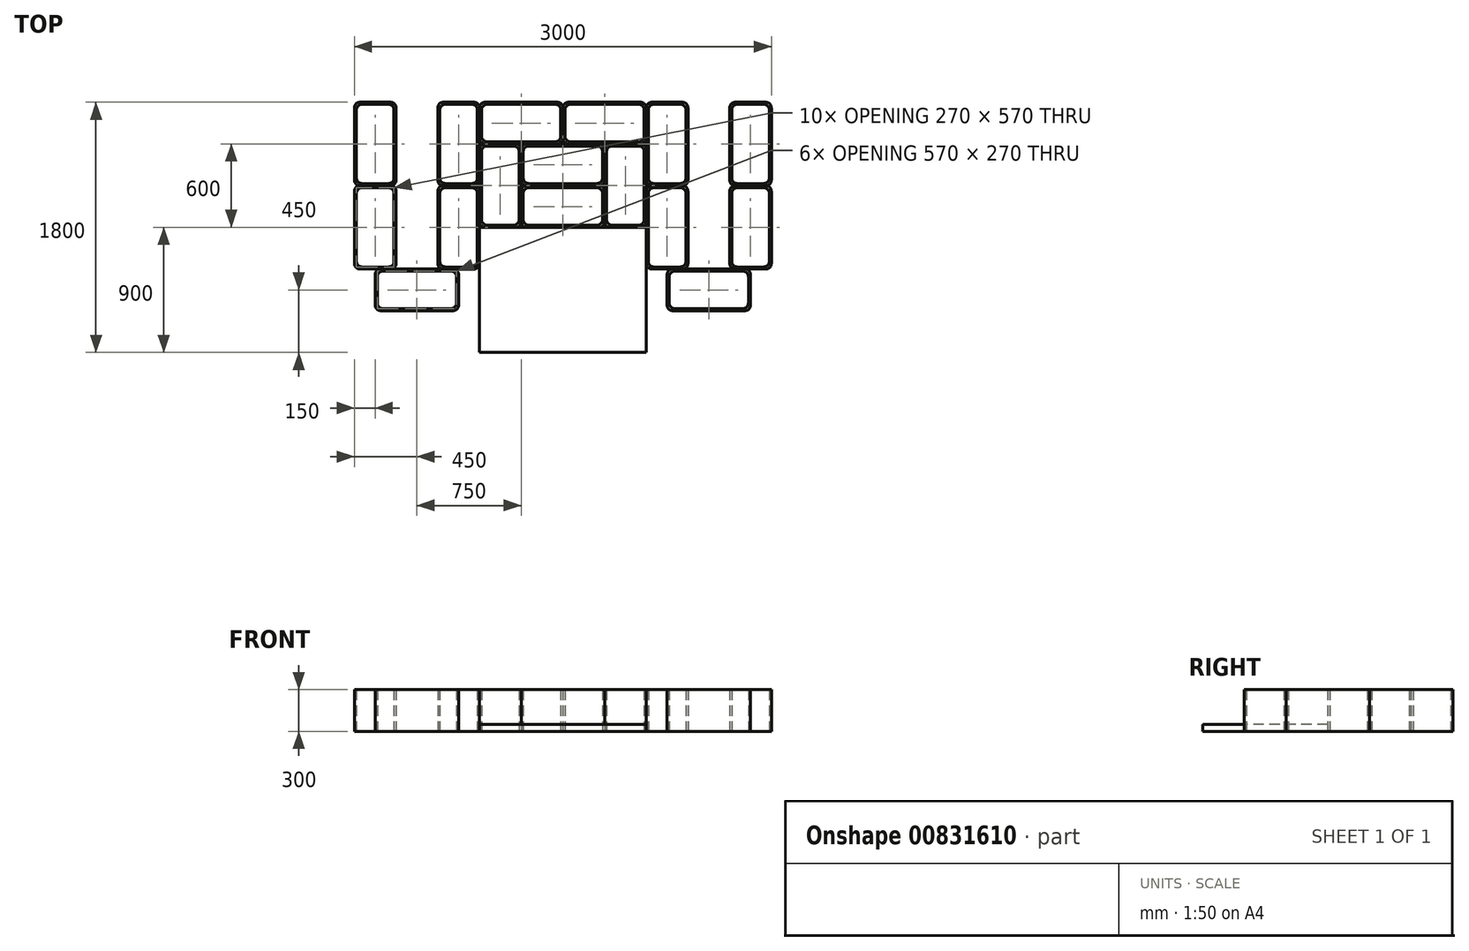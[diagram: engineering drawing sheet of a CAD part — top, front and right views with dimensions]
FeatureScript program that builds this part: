
annotation { "Feature Type Name" : "Feature", "Feature Type Description" : "" }
export const myFeature = defineFeature(function(context is Context, id is Id, definition is map)
    precondition{}
    {
        {
            var Q0;
            Q0=qCreatedBy(makeId("Top.planeOp"),FACE);
            var sketch = newSketch(context, id + "F0", { "sketchPlane" : qUnion([Q0])});
            skLineSegment(sketch, "E0.bottom", {"start": v(260, 150) * mm, "end": v(-260, 150) * mm});
            skLineSegment(sketch, "E0.top", {"start": v(260, -150) * mm, "end": v(-260, -150) * mm});
            skLineSegment(sketch, "E0.left", {"start": v(300, 110) * mm, "end": v(300, -110) * mm});
            skLineSegment(sketch, "E0.right", {"start": v(-300, 110) * mm, "end": v(-300, -110) * mm});
            skPoint(sketch, "E0.middle", {"position": v(0, 0) * mm});
            skArc(sketch, "E1", {"start": v(-300, -110) * mm, "mid": v(-288.28, -138.28) * mm, "end": v(-260, -150) * mm});
            skArc(sketch, "E2", {"start": v(260, -150) * mm, "mid": v(288.28, -138.28) * mm, "end": v(300, -110) * mm});
            skArc(sketch, "E3", {"start": v(300, 110) * mm, "mid": v(288.28, 138.28) * mm, "end": v(260, 150) * mm});
            skArc(sketch, "E4", {"start": v(-260, 150) * mm, "mid": v(-288.28, 138.28) * mm, "end": v(-300, 110) * mm});
            skPoint(sketch, "E5.orphan", {"position": v(-300, -150) * mm});
            skPoint(sketch, "E6.orphan", {"position": v(300, -150) * mm});
            skPoint(sketch, "E7.orphan", {"position": v(300, 150) * mm});
            skPoint(sketch, "E8.orphan", {"position": v(-300, 150) * mm});
            skSolve(sketch);
        }
        {
            var Q0;
            Q0=makeQuery(id+"F0.imprint","IMPRINT",FACE,{"disambiguationData":[TD([[makeQuery(id+"F0.imprint","IMPRINT",EDGE,{"derivedFrom":sQuery(id+"F0.wireOp",EDGE,"E0.bottom")}),1.0]])]});
            var sketch = newSketch(context, id + "F1", { "sketchPlane" : qUnion([Q0])});
            skLineSegment(sketch, "E9.bottom", {"start": v(245, 135) * mm, "end": v(-245, 135) * mm});
            skLineSegment(sketch, "E9.top", {"start": v(245, -135) * mm, "end": v(-245, -135) * mm});
            skLineSegment(sketch, "E9.left", {"start": v(285, 95) * mm, "end": v(285, -95) * mm});
            skLineSegment(sketch, "E9.right", {"start": v(-285, 95) * mm, "end": v(-285, -95) * mm});
            skPoint(sketch, "E9.middle", {"position": v(0, 0) * mm});
            skArc(sketch, "E10", {"start": v(-285, -95) * mm, "mid": v(-273.28, -123.28) * mm, "end": v(-245, -135) * mm});
            skArc(sketch, "E11", {"start": v(245, -135) * mm, "mid": v(273.28, -123.28) * mm, "end": v(285, -95) * mm});
            skPoint(sketch, "E12.orphan", {"position": v(-285, -135) * mm});
            skPoint(sketch, "E13.orphan", {"position": v(285, -135) * mm});
            skArc(sketch, "E14", {"start": v(285, 95) * mm, "mid": v(273.28, 123.28) * mm, "end": v(245, 135) * mm});
            skArc(sketch, "E15", {"start": v(-245, 135) * mm, "mid": v(-273.28, 123.28) * mm, "end": v(-285, 95) * mm});
            skPoint(sketch, "E16.orphan", {"position": v(285, 135) * mm});
            skPoint(sketch, "E17.orphan", {"position": v(-285, 135) * mm});
            skSolve(sketch);
        }
        {
            var Q0;
            Q0=makeQuery(id+"F1.imprint","IMPRINT",FACE,{"disambiguationData":[TD([[makeQuery(id+"F1.imprint","IMPRINT",EDGE,{"derivedFrom":sQuery(id+"F1.wireOp",EDGE,"E9.bottom")}),-1.0]])]});
            extrude(context, id + "F2", {"entities" : qUnion([Q0]), "depth" : 300 * mm, "offsetDistance" : 25 * mm});
        }
        {
            var Q0;
            Q0=makeQuery(id+"F2.opExtrude","SWEPT_BODY",BODY,{"disambiguationData":[OSD([sQuery(id+"F0.wireOp",EDGE,"E0.bottom"),sQuery(id+"F0.wireOp",EDGE,"E0.top"),sQuery(id+"F0.wireOp",EDGE,"E0.left"),sQuery(id+"F0.wireOp",EDGE,"E0.right"),sQuery(id+"F0.wireOp",EDGE,"E1"),sQuery(id+"F0.wireOp",EDGE,"E2"),sQuery(id+"F0.wireOp",EDGE,"E3"),sQuery(id+"F0.wireOp",EDGE,"E4"),sQuery(id+"F1.wireOp",EDGE,"E9.bottom"),sQuery(id+"F1.wireOp",EDGE,"E9.top"),sQuery(id+"F1.wireOp",EDGE,"E9.left"),sQuery(id+"F1.wireOp",EDGE,"E9.right"),sQuery(id+"F1.wireOp",EDGE,"E10"),sQuery(id+"F1.wireOp",EDGE,"E11"),sQuery(id+"F1.wireOp",EDGE,"E14"),sQuery(id+"F1.wireOp",EDGE,"E15")])]});
            transform(context, id + "F3", {"entities" : qUnion([Q0]), "transformType" : TransformType.TRANSLATION_3D, "dx" : 900 * mm, "dy" : 0 * mm, "dz" : 0 * mm, "makeCopy" : true});
        }
        {
            var Q0;
            Q0=makeQuery(id+"F3.opPattern","COPY",BODY,{"derivedFrom":makeQuery(id+"F2.opExtrude","SWEPT_BODY",BODY,{"disambiguationData":[OSD([sQuery(id+"F0.wireOp",EDGE,"E0.bottom"),sQuery(id+"F0.wireOp",EDGE,"E0.top"),sQuery(id+"F0.wireOp",EDGE,"E0.left"),sQuery(id+"F0.wireOp",EDGE,"E0.right"),sQuery(id+"F0.wireOp",EDGE,"E1"),sQuery(id+"F0.wireOp",EDGE,"E2"),sQuery(id+"F0.wireOp",EDGE,"E3"),sQuery(id+"F0.wireOp",EDGE,"E4"),sQuery(id+"F1.wireOp",EDGE,"E9.bottom"),sQuery(id+"F1.wireOp",EDGE,"E9.top"),sQuery(id+"F1.wireOp",EDGE,"E9.left"),sQuery(id+"F1.wireOp",EDGE,"E9.right"),sQuery(id+"F1.wireOp",EDGE,"E10"),sQuery(id+"F1.wireOp",EDGE,"E11"),sQuery(id+"F1.wireOp",EDGE,"E14"),sQuery(id+"F1.wireOp",EDGE,"E15")])]}),"instanceName":"1"});
            var Q1;
            Q1=makeQuery(id+"F3.opPattern","COPY",EDGE,{"derivedFrom":makeQuery(id+"F2.opExtrude","SWEPT_EDGE",EDGE,{"disambiguationData":[OSD([sQuery(id+"F1.wireOp",EDGE,"E9.right"),sQuery(id+"F1.wireOp",EDGE,"E15")])]}),"instanceName":"1"});
            transform(context, id + "F4", {"entities" : qUnion([Q0]), "transformType" : TransformType.ROTATION, "transformAxis" : qUnion([Q1]), "angle" : 90 * degree, "makeCopy" : true});
        }
        {
            var Q0;
            Q0=makeQuery(id+"F4.opPattern","COPY",BODY,{"derivedFrom":makeQuery(id+"F3.opPattern","COPY",BODY,{"derivedFrom":makeQuery(id+"F2.opExtrude","SWEPT_BODY",BODY,{"disambiguationData":[OSD([sQuery(id+"F0.wireOp",EDGE,"E0.bottom"),sQuery(id+"F0.wireOp",EDGE,"E0.top"),sQuery(id+"F0.wireOp",EDGE,"E0.left"),sQuery(id+"F0.wireOp",EDGE,"E0.right"),sQuery(id+"F0.wireOp",EDGE,"E1"),sQuery(id+"F0.wireOp",EDGE,"E2"),sQuery(id+"F0.wireOp",EDGE,"E3"),sQuery(id+"F0.wireOp",EDGE,"E4"),sQuery(id+"F1.wireOp",EDGE,"E9.bottom"),sQuery(id+"F1.wireOp",EDGE,"E9.top"),sQuery(id+"F1.wireOp",EDGE,"E9.left"),sQuery(id+"F1.wireOp",EDGE,"E9.right"),sQuery(id+"F1.wireOp",EDGE,"E10"),sQuery(id+"F1.wireOp",EDGE,"E11"),sQuery(id+"F1.wireOp",EDGE,"E14"),sQuery(id+"F1.wireOp",EDGE,"E15")])]}),"instanceName":"1"}),"instanceName":"1"});
            transform(context, id + "F5", {"entities" : qUnion([Q0]), "transformType" : TransformType.TRANSLATION_3D, "dx" : -70 * mm, "dy" : 40 * mm, "dz" : 0 * mm, "makeCopy" : false});
        }
        {
            var Q0;
            Q0=makeQuery(id+"F3.opPattern","COPY",BODY,{"derivedFrom":makeQuery(id+"F2.opExtrude","SWEPT_BODY",BODY,{"disambiguationData":[OSD([sQuery(id+"F0.wireOp",EDGE,"E0.bottom"),sQuery(id+"F0.wireOp",EDGE,"E0.top"),sQuery(id+"F0.wireOp",EDGE,"E0.left"),sQuery(id+"F0.wireOp",EDGE,"E0.right"),sQuery(id+"F0.wireOp",EDGE,"E1"),sQuery(id+"F0.wireOp",EDGE,"E2"),sQuery(id+"F0.wireOp",EDGE,"E3"),sQuery(id+"F0.wireOp",EDGE,"E4"),sQuery(id+"F1.wireOp",EDGE,"E9.bottom"),sQuery(id+"F1.wireOp",EDGE,"E9.top"),sQuery(id+"F1.wireOp",EDGE,"E9.left"),sQuery(id+"F1.wireOp",EDGE,"E9.right"),sQuery(id+"F1.wireOp",EDGE,"E10"),sQuery(id+"F1.wireOp",EDGE,"E11"),sQuery(id+"F1.wireOp",EDGE,"E14"),sQuery(id+"F1.wireOp",EDGE,"E15")])]}),"instanceName":"1"});
            transform(context, id + "F6", {"entities" : qUnion([Q0]), "transformType" : TransformType.TRANSLATION_3D, "dx" : -1500 * mm, "dy" : 0 * mm, "dz" : 0 * mm, "makeCopy" : false});
        }
        {
            var Q0;
            Q0=makeQuery(id+"F3.opPattern","COPY",BODY,{"derivedFrom":makeQuery(id+"F2.opExtrude","SWEPT_BODY",BODY,{"disambiguationData":[OSD([sQuery(id+"F0.wireOp",EDGE,"E0.bottom"),sQuery(id+"F0.wireOp",EDGE,"E0.top"),sQuery(id+"F0.wireOp",EDGE,"E0.left"),sQuery(id+"F0.wireOp",EDGE,"E0.right"),sQuery(id+"F0.wireOp",EDGE,"E1"),sQuery(id+"F0.wireOp",EDGE,"E2"),sQuery(id+"F0.wireOp",EDGE,"E3"),sQuery(id+"F0.wireOp",EDGE,"E4"),sQuery(id+"F1.wireOp",EDGE,"E9.bottom"),sQuery(id+"F1.wireOp",EDGE,"E9.top"),sQuery(id+"F1.wireOp",EDGE,"E9.left"),sQuery(id+"F1.wireOp",EDGE,"E9.right"),sQuery(id+"F1.wireOp",EDGE,"E10"),sQuery(id+"F1.wireOp",EDGE,"E11"),sQuery(id+"F1.wireOp",EDGE,"E14"),sQuery(id+"F1.wireOp",EDGE,"E15")])]}),"instanceName":"1"});
            transform(context, id + "F7", {"entities" : qUnion([Q0]), "transformType" : TransformType.TRANSLATION_3D, "dx" : 300 * mm, "dy" : -300 * mm, "dz" : 0 * mm, "makeCopy" : true});
        }
        {
            var Q0;
            Q0=makeQuery(id+"F4.opPattern","COPY",BODY,{"derivedFrom":makeQuery(id+"F3.opPattern","COPY",BODY,{"derivedFrom":makeQuery(id+"F2.opExtrude","SWEPT_BODY",BODY,{"disambiguationData":[OSD([sQuery(id+"F0.wireOp",EDGE,"E0.bottom"),sQuery(id+"F0.wireOp",EDGE,"E0.top"),sQuery(id+"F0.wireOp",EDGE,"E0.left"),sQuery(id+"F0.wireOp",EDGE,"E0.right"),sQuery(id+"F0.wireOp",EDGE,"E1"),sQuery(id+"F0.wireOp",EDGE,"E2"),sQuery(id+"F0.wireOp",EDGE,"E3"),sQuery(id+"F0.wireOp",EDGE,"E4"),sQuery(id+"F1.wireOp",EDGE,"E9.bottom"),sQuery(id+"F1.wireOp",EDGE,"E9.top"),sQuery(id+"F1.wireOp",EDGE,"E9.left"),sQuery(id+"F1.wireOp",EDGE,"E9.right"),sQuery(id+"F1.wireOp",EDGE,"E10"),sQuery(id+"F1.wireOp",EDGE,"E11"),sQuery(id+"F1.wireOp",EDGE,"E14"),sQuery(id+"F1.wireOp",EDGE,"E15")])]}),"instanceName":"1"}),"instanceName":"1"});
            transform(context, id + "F8", {"entities" : qUnion([Q0]), "transformType" : TransformType.TRANSLATION_3D, "dx" : 300 * mm, "dy" : 0 * mm, "dz" : 0 * mm, "makeCopy" : true});
        }
        {
            var Q0;
            Q0=makeQuery(id+"F7.opPattern","COPY",BODY,{"derivedFrom":makeQuery(id+"F3.opPattern","COPY",BODY,{"derivedFrom":makeQuery(id+"F2.opExtrude","SWEPT_BODY",BODY,{"disambiguationData":[OSD([sQuery(id+"F0.wireOp",EDGE,"E0.bottom"),sQuery(id+"F0.wireOp",EDGE,"E0.top"),sQuery(id+"F0.wireOp",EDGE,"E0.left"),sQuery(id+"F0.wireOp",EDGE,"E0.right"),sQuery(id+"F0.wireOp",EDGE,"E1"),sQuery(id+"F0.wireOp",EDGE,"E2"),sQuery(id+"F0.wireOp",EDGE,"E3"),sQuery(id+"F0.wireOp",EDGE,"E4"),sQuery(id+"F1.wireOp",EDGE,"E9.bottom"),sQuery(id+"F1.wireOp",EDGE,"E9.top"),sQuery(id+"F1.wireOp",EDGE,"E9.left"),sQuery(id+"F1.wireOp",EDGE,"E9.right"),sQuery(id+"F1.wireOp",EDGE,"E10"),sQuery(id+"F1.wireOp",EDGE,"E11"),sQuery(id+"F1.wireOp",EDGE,"E14"),sQuery(id+"F1.wireOp",EDGE,"E15")])]}),"instanceName":"1"}),"instanceName":"1"});
            var Q1;
            Q1=makeQuery(id+"F4.opPattern","COPY",BODY,{"derivedFrom":makeQuery(id+"F3.opPattern","COPY",BODY,{"derivedFrom":makeQuery(id+"F2.opExtrude","SWEPT_BODY",BODY,{"disambiguationData":[OSD([sQuery(id+"F0.wireOp",EDGE,"E0.bottom"),sQuery(id+"F0.wireOp",EDGE,"E0.top"),sQuery(id+"F0.wireOp",EDGE,"E0.left"),sQuery(id+"F0.wireOp",EDGE,"E0.right"),sQuery(id+"F0.wireOp",EDGE,"E1"),sQuery(id+"F0.wireOp",EDGE,"E2"),sQuery(id+"F0.wireOp",EDGE,"E3"),sQuery(id+"F0.wireOp",EDGE,"E4"),sQuery(id+"F1.wireOp",EDGE,"E9.bottom"),sQuery(id+"F1.wireOp",EDGE,"E9.top"),sQuery(id+"F1.wireOp",EDGE,"E9.left"),sQuery(id+"F1.wireOp",EDGE,"E9.right"),sQuery(id+"F1.wireOp",EDGE,"E10"),sQuery(id+"F1.wireOp",EDGE,"E11"),sQuery(id+"F1.wireOp",EDGE,"E14"),sQuery(id+"F1.wireOp",EDGE,"E15")])]}),"instanceName":"1"}),"instanceName":"1"});
            transform(context, id + "F9", {"entities" : qUnion([Q0, Q1]), "transformType" : TransformType.TRANSLATION_3D, "dx" : 900 * mm, "dy" : -300 * mm, "dz" : 0 * mm, "makeCopy" : true});
        }
        {
            var Q0;
            Q0=makeQuery(id+"F4.opPattern","COPY",BODY,{"derivedFrom":makeQuery(id+"F3.opPattern","COPY",BODY,{"derivedFrom":makeQuery(id+"F2.opExtrude","SWEPT_BODY",BODY,{"disambiguationData":[OSD([sQuery(id+"F0.wireOp",EDGE,"E0.bottom"),sQuery(id+"F0.wireOp",EDGE,"E0.top"),sQuery(id+"F0.wireOp",EDGE,"E0.left"),sQuery(id+"F0.wireOp",EDGE,"E0.right"),sQuery(id+"F0.wireOp",EDGE,"E1"),sQuery(id+"F0.wireOp",EDGE,"E2"),sQuery(id+"F0.wireOp",EDGE,"E3"),sQuery(id+"F0.wireOp",EDGE,"E4"),sQuery(id+"F1.wireOp",EDGE,"E9.bottom"),sQuery(id+"F1.wireOp",EDGE,"E9.top"),sQuery(id+"F1.wireOp",EDGE,"E9.left"),sQuery(id+"F1.wireOp",EDGE,"E9.right"),sQuery(id+"F1.wireOp",EDGE,"E10"),sQuery(id+"F1.wireOp",EDGE,"E11"),sQuery(id+"F1.wireOp",EDGE,"E14"),sQuery(id+"F1.wireOp",EDGE,"E15")])]}),"instanceName":"1"}),"instanceName":"1"});
            transform(context, id + "F10", {"entities" : qUnion([Q0]), "transformType" : TransformType.TRANSLATION_3D, "dx" : -300 * mm, "dy" : -300 * mm, "dz" : 0 * mm, "makeCopy" : true});
        }
        {
            var Q0;
            Q0=makeQuery(id+"F9.opPattern","COPY",BODY,{"derivedFrom":makeQuery(id+"F4.opPattern","COPY",BODY,{"derivedFrom":makeQuery(id+"F3.opPattern","COPY",BODY,{"derivedFrom":makeQuery(id+"F2.opExtrude","SWEPT_BODY",BODY,{"disambiguationData":[OSD([sQuery(id+"F0.wireOp",EDGE,"E0.bottom"),sQuery(id+"F0.wireOp",EDGE,"E0.top"),sQuery(id+"F0.wireOp",EDGE,"E0.left"),sQuery(id+"F0.wireOp",EDGE,"E0.right"),sQuery(id+"F0.wireOp",EDGE,"E1"),sQuery(id+"F0.wireOp",EDGE,"E2"),sQuery(id+"F0.wireOp",EDGE,"E3"),sQuery(id+"F0.wireOp",EDGE,"E4"),sQuery(id+"F1.wireOp",EDGE,"E9.bottom"),sQuery(id+"F1.wireOp",EDGE,"E9.top"),sQuery(id+"F1.wireOp",EDGE,"E9.left"),sQuery(id+"F1.wireOp",EDGE,"E9.right"),sQuery(id+"F1.wireOp",EDGE,"E10"),sQuery(id+"F1.wireOp",EDGE,"E11"),sQuery(id+"F1.wireOp",EDGE,"E14"),sQuery(id+"F1.wireOp",EDGE,"E15")])]}),"instanceName":"1"}),"instanceName":"1"}),"instanceName":"1"});
            transform(context, id + "F11", {"entities" : qUnion([Q0]), "transformType" : TransformType.TRANSLATION_3D, "dx" : -2100 * mm, "dy" : 0 * mm, "dz" : 0 * mm, "makeCopy" : false});
        }
        {
            var Q0;
            Q0=makeQuery(id+"F7.opPattern","COPY",BODY,{"derivedFrom":makeQuery(id+"F3.opPattern","COPY",BODY,{"derivedFrom":makeQuery(id+"F2.opExtrude","SWEPT_BODY",BODY,{"disambiguationData":[OSD([sQuery(id+"F0.wireOp",EDGE,"E0.bottom"),sQuery(id+"F0.wireOp",EDGE,"E0.top"),sQuery(id+"F0.wireOp",EDGE,"E0.left"),sQuery(id+"F0.wireOp",EDGE,"E0.right"),sQuery(id+"F0.wireOp",EDGE,"E1"),sQuery(id+"F0.wireOp",EDGE,"E2"),sQuery(id+"F0.wireOp",EDGE,"E3"),sQuery(id+"F0.wireOp",EDGE,"E4"),sQuery(id+"F1.wireOp",EDGE,"E9.bottom"),sQuery(id+"F1.wireOp",EDGE,"E9.top"),sQuery(id+"F1.wireOp",EDGE,"E9.left"),sQuery(id+"F1.wireOp",EDGE,"E9.right"),sQuery(id+"F1.wireOp",EDGE,"E10"),sQuery(id+"F1.wireOp",EDGE,"E11"),sQuery(id+"F1.wireOp",EDGE,"E14"),sQuery(id+"F1.wireOp",EDGE,"E15")])]}),"instanceName":"1"}),"instanceName":"1"});
            transform(context, id + "F12", {"entities" : qUnion([Q0]), "transformType" : TransformType.TRANSLATION_3D, "dx" : 0 * mm, "dy" : -300 * mm, "dz" : 0 * mm, "makeCopy" : true});
        }
        {
            var Q0;
            Q0=makeQuery(id+"F8.opPattern","COPY",BODY,{"derivedFrom":makeQuery(id+"F4.opPattern","COPY",BODY,{"derivedFrom":makeQuery(id+"F3.opPattern","COPY",BODY,{"derivedFrom":makeQuery(id+"F2.opExtrude","SWEPT_BODY",BODY,{"disambiguationData":[OSD([sQuery(id+"F0.wireOp",EDGE,"E0.bottom"),sQuery(id+"F0.wireOp",EDGE,"E0.top"),sQuery(id+"F0.wireOp",EDGE,"E0.left"),sQuery(id+"F0.wireOp",EDGE,"E0.right"),sQuery(id+"F0.wireOp",EDGE,"E1"),sQuery(id+"F0.wireOp",EDGE,"E2"),sQuery(id+"F0.wireOp",EDGE,"E3"),sQuery(id+"F0.wireOp",EDGE,"E4"),sQuery(id+"F1.wireOp",EDGE,"E9.bottom"),sQuery(id+"F1.wireOp",EDGE,"E9.top"),sQuery(id+"F1.wireOp",EDGE,"E9.left"),sQuery(id+"F1.wireOp",EDGE,"E9.right"),sQuery(id+"F1.wireOp",EDGE,"E10"),sQuery(id+"F1.wireOp",EDGE,"E11"),sQuery(id+"F1.wireOp",EDGE,"E14"),sQuery(id+"F1.wireOp",EDGE,"E15")])]}),"instanceName":"1"}),"instanceName":"1"}),"instanceName":"1"});
            transform(context, id + "F13", {"entities" : qUnion([Q0]), "transformType" : TransformType.TRANSLATION_3D, "dx" : -1800 * mm, "dy" : 0 * mm, "dz" : 0 * mm, "makeCopy" : true});
        }
        {
            var Q0;
            Q0=makeQuery(id+"F13.opPattern","COPY",BODY,{"derivedFrom":makeQuery(id+"F8.opPattern","COPY",BODY,{"derivedFrom":makeQuery(id+"F4.opPattern","COPY",BODY,{"derivedFrom":makeQuery(id+"F3.opPattern","COPY",BODY,{"derivedFrom":makeQuery(id+"F2.opExtrude","SWEPT_BODY",BODY,{"disambiguationData":[OSD([sQuery(id+"F0.wireOp",EDGE,"E0.bottom"),sQuery(id+"F0.wireOp",EDGE,"E0.top"),sQuery(id+"F0.wireOp",EDGE,"E0.left"),sQuery(id+"F0.wireOp",EDGE,"E0.right"),sQuery(id+"F0.wireOp",EDGE,"E1"),sQuery(id+"F0.wireOp",EDGE,"E2"),sQuery(id+"F0.wireOp",EDGE,"E3"),sQuery(id+"F0.wireOp",EDGE,"E4"),sQuery(id+"F1.wireOp",EDGE,"E9.bottom"),sQuery(id+"F1.wireOp",EDGE,"E9.top"),sQuery(id+"F1.wireOp",EDGE,"E9.left"),sQuery(id+"F1.wireOp",EDGE,"E9.right"),sQuery(id+"F1.wireOp",EDGE,"E10"),sQuery(id+"F1.wireOp",EDGE,"E11"),sQuery(id+"F1.wireOp",EDGE,"E14"),sQuery(id+"F1.wireOp",EDGE,"E15")])]}),"instanceName":"1"}),"instanceName":"1"}),"instanceName":"1"}),"instanceName":"1"});
            transform(context, id + "F14", {"entities" : qUnion([Q0]), "transformType" : TransformType.TRANSLATION_3D, "dx" : -300 * mm, "dy" : 0 * mm, "dz" : 0 * mm, "makeCopy" : true});
        }
        {
            var Q0;
            Q0=makeQuery(id+"F9.opPattern","COPY",BODY,{"derivedFrom":makeQuery(id+"F7.opPattern","COPY",BODY,{"derivedFrom":makeQuery(id+"F3.opPattern","COPY",BODY,{"derivedFrom":makeQuery(id+"F2.opExtrude","SWEPT_BODY",BODY,{"disambiguationData":[OSD([sQuery(id+"F0.wireOp",EDGE,"E0.bottom"),sQuery(id+"F0.wireOp",EDGE,"E0.top"),sQuery(id+"F0.wireOp",EDGE,"E0.left"),sQuery(id+"F0.wireOp",EDGE,"E0.right"),sQuery(id+"F0.wireOp",EDGE,"E1"),sQuery(id+"F0.wireOp",EDGE,"E2"),sQuery(id+"F0.wireOp",EDGE,"E3"),sQuery(id+"F0.wireOp",EDGE,"E4"),sQuery(id+"F1.wireOp",EDGE,"E9.bottom"),sQuery(id+"F1.wireOp",EDGE,"E9.top"),sQuery(id+"F1.wireOp",EDGE,"E9.left"),sQuery(id+"F1.wireOp",EDGE,"E9.right"),sQuery(id+"F1.wireOp",EDGE,"E10"),sQuery(id+"F1.wireOp",EDGE,"E11"),sQuery(id+"F1.wireOp",EDGE,"E14"),sQuery(id+"F1.wireOp",EDGE,"E15")])]}),"instanceName":"1"}),"instanceName":"1"}),"instanceName":"1"});
            transform(context, id + "F15", {"entities" : qUnion([Q0]), "transformType" : TransformType.TRANSLATION_3D, "dx" : -1800 * mm, "dy" : 0 * mm, "dz" : 0 * mm, "makeCopy" : true});
        }
        {
            var Q0;
            Q0=makeQuery(id+"F15.opPattern","COPY",BODY,{"derivedFrom":makeQuery(id+"F9.opPattern","COPY",BODY,{"derivedFrom":makeQuery(id+"F7.opPattern","COPY",BODY,{"derivedFrom":makeQuery(id+"F3.opPattern","COPY",BODY,{"derivedFrom":makeQuery(id+"F2.opExtrude","SWEPT_BODY",BODY,{"disambiguationData":[OSD([sQuery(id+"F0.wireOp",EDGE,"E0.bottom"),sQuery(id+"F0.wireOp",EDGE,"E0.top"),sQuery(id+"F0.wireOp",EDGE,"E0.left"),sQuery(id+"F0.wireOp",EDGE,"E0.right"),sQuery(id+"F0.wireOp",EDGE,"E1"),sQuery(id+"F0.wireOp",EDGE,"E2"),sQuery(id+"F0.wireOp",EDGE,"E3"),sQuery(id+"F0.wireOp",EDGE,"E4"),sQuery(id+"F1.wireOp",EDGE,"E9.bottom"),sQuery(id+"F1.wireOp",EDGE,"E9.top"),sQuery(id+"F1.wireOp",EDGE,"E9.left"),sQuery(id+"F1.wireOp",EDGE,"E9.right"),sQuery(id+"F1.wireOp",EDGE,"E10"),sQuery(id+"F1.wireOp",EDGE,"E11"),sQuery(id+"F1.wireOp",EDGE,"E14"),sQuery(id+"F1.wireOp",EDGE,"E15")])]}),"instanceName":"1"}),"instanceName":"1"}),"instanceName":"1"}),"instanceName":"1"});
            transform(context, id + "F16", {"entities" : qUnion([Q0]), "transformType" : TransformType.TRANSLATION_3D, "dx" : 0 * mm, "dy" : -600 * mm, "dz" : 0 * mm, "makeCopy" : false});
        }
        {
            var Q0;
            Q0=makeQuery(id+"F13.opPattern","COPY",BODY,{"derivedFrom":makeQuery(id+"F8.opPattern","COPY",BODY,{"derivedFrom":makeQuery(id+"F4.opPattern","COPY",BODY,{"derivedFrom":makeQuery(id+"F3.opPattern","COPY",BODY,{"derivedFrom":makeQuery(id+"F2.opExtrude","SWEPT_BODY",BODY,{"disambiguationData":[OSD([sQuery(id+"F0.wireOp",EDGE,"E0.bottom"),sQuery(id+"F0.wireOp",EDGE,"E0.top"),sQuery(id+"F0.wireOp",EDGE,"E0.left"),sQuery(id+"F0.wireOp",EDGE,"E0.right"),sQuery(id+"F0.wireOp",EDGE,"E1"),sQuery(id+"F0.wireOp",EDGE,"E2"),sQuery(id+"F0.wireOp",EDGE,"E3"),sQuery(id+"F0.wireOp",EDGE,"E4"),sQuery(id+"F1.wireOp",EDGE,"E9.bottom"),sQuery(id+"F1.wireOp",EDGE,"E9.top"),sQuery(id+"F1.wireOp",EDGE,"E9.left"),sQuery(id+"F1.wireOp",EDGE,"E9.right"),sQuery(id+"F1.wireOp",EDGE,"E10"),sQuery(id+"F1.wireOp",EDGE,"E11"),sQuery(id+"F1.wireOp",EDGE,"E14"),sQuery(id+"F1.wireOp",EDGE,"E15")])]}),"instanceName":"1"}),"instanceName":"1"}),"instanceName":"1"}),"instanceName":"1"});
            transform(context, id + "F17", {"entities" : qUnion([Q0]), "transformType" : TransformType.TRANSLATION_3D, "dx" : -300 * mm, "dy" : -600 * mm, "dz" : 0 * mm, "makeCopy" : false});
        }
        {
            var Q0;
            Q0=makeQuery(id+"F15.opPattern","COPY",BODY,{"derivedFrom":makeQuery(id+"F9.opPattern","COPY",BODY,{"derivedFrom":makeQuery(id+"F7.opPattern","COPY",BODY,{"derivedFrom":makeQuery(id+"F3.opPattern","COPY",BODY,{"derivedFrom":makeQuery(id+"F2.opExtrude","SWEPT_BODY",BODY,{"disambiguationData":[OSD([sQuery(id+"F0.wireOp",EDGE,"E0.bottom"),sQuery(id+"F0.wireOp",EDGE,"E0.top"),sQuery(id+"F0.wireOp",EDGE,"E0.left"),sQuery(id+"F0.wireOp",EDGE,"E0.right"),sQuery(id+"F0.wireOp",EDGE,"E1"),sQuery(id+"F0.wireOp",EDGE,"E2"),sQuery(id+"F0.wireOp",EDGE,"E3"),sQuery(id+"F0.wireOp",EDGE,"E4"),sQuery(id+"F1.wireOp",EDGE,"E9.bottom"),sQuery(id+"F1.wireOp",EDGE,"E9.top"),sQuery(id+"F1.wireOp",EDGE,"E9.left"),sQuery(id+"F1.wireOp",EDGE,"E9.right"),sQuery(id+"F1.wireOp",EDGE,"E10"),sQuery(id+"F1.wireOp",EDGE,"E11"),sQuery(id+"F1.wireOp",EDGE,"E14"),sQuery(id+"F1.wireOp",EDGE,"E15")])]}),"instanceName":"1"}),"instanceName":"1"}),"instanceName":"1"}),"instanceName":"1"});
            transform(context, id + "F18", {"entities" : qUnion([Q0]), "transformType" : TransformType.TRANSLATION_3D, "dx" : 150 * mm, "dy" : 0 * mm, "dz" : 0 * mm, "makeCopy" : false});
        }
        {
            var Q0;
            Q0=makeQuery(id+"F9.opPattern","COPY",BODY,{"derivedFrom":makeQuery(id+"F7.opPattern","COPY",BODY,{"derivedFrom":makeQuery(id+"F3.opPattern","COPY",BODY,{"derivedFrom":makeQuery(id+"F2.opExtrude","SWEPT_BODY",BODY,{"disambiguationData":[OSD([sQuery(id+"F0.wireOp",EDGE,"E0.bottom"),sQuery(id+"F0.wireOp",EDGE,"E0.top"),sQuery(id+"F0.wireOp",EDGE,"E0.left"),sQuery(id+"F0.wireOp",EDGE,"E0.right"),sQuery(id+"F0.wireOp",EDGE,"E1"),sQuery(id+"F0.wireOp",EDGE,"E2"),sQuery(id+"F0.wireOp",EDGE,"E3"),sQuery(id+"F0.wireOp",EDGE,"E4"),sQuery(id+"F1.wireOp",EDGE,"E9.bottom"),sQuery(id+"F1.wireOp",EDGE,"E9.top"),sQuery(id+"F1.wireOp",EDGE,"E9.left"),sQuery(id+"F1.wireOp",EDGE,"E9.right"),sQuery(id+"F1.wireOp",EDGE,"E10"),sQuery(id+"F1.wireOp",EDGE,"E11"),sQuery(id+"F1.wireOp",EDGE,"E14"),sQuery(id+"F1.wireOp",EDGE,"E15")])]}),"instanceName":"1"}),"instanceName":"1"}),"instanceName":"1"});
            transform(context, id + "F19", {"entities" : qUnion([Q0]), "transformType" : TransformType.TRANSLATION_3D, "dx" : -150 * mm, "dy" : -600 * mm, "dz" : 0 * mm, "makeCopy" : false});
        }
        {
            var Q0;
            Q0=makeQuery(id+"F4.opPattern","COPY",BODY,{"derivedFrom":makeQuery(id+"F3.opPattern","COPY",BODY,{"derivedFrom":makeQuery(id+"F2.opExtrude","SWEPT_BODY",BODY,{"disambiguationData":[OSD([sQuery(id+"F0.wireOp",EDGE,"E0.bottom"),sQuery(id+"F0.wireOp",EDGE,"E0.top"),sQuery(id+"F0.wireOp",EDGE,"E0.left"),sQuery(id+"F0.wireOp",EDGE,"E0.right"),sQuery(id+"F0.wireOp",EDGE,"E1"),sQuery(id+"F0.wireOp",EDGE,"E2"),sQuery(id+"F0.wireOp",EDGE,"E3"),sQuery(id+"F0.wireOp",EDGE,"E4"),sQuery(id+"F1.wireOp",EDGE,"E9.bottom"),sQuery(id+"F1.wireOp",EDGE,"E9.top"),sQuery(id+"F1.wireOp",EDGE,"E9.left"),sQuery(id+"F1.wireOp",EDGE,"E9.right"),sQuery(id+"F1.wireOp",EDGE,"E10"),sQuery(id+"F1.wireOp",EDGE,"E11"),sQuery(id+"F1.wireOp",EDGE,"E14"),sQuery(id+"F1.wireOp",EDGE,"E15")])]}),"instanceName":"1"}),"instanceName":"1"});
            transform(context, id + "F20", {"entities" : qUnion([Q0]), "transformType" : TransformType.TRANSLATION_3D, "dx" : 300 * mm, "dy" : -600 * mm, "dz" : 0 * mm, "makeCopy" : false});
        }
        {
            var Q0;
            Q0=makeQuery(id+"F0.imprint","IMPRINT",FACE,{"disambiguationData":[TD([[makeQuery(id+"F0.imprint","IMPRINT",EDGE,{"derivedFrom":sQuery(id+"F0.wireOp",EDGE,"E0.bottom")}),1.0]])]});
            var sketch = newSketch(context, id + "F21", { "sketchPlane" : qUnion([Q0])});
            skLineSegment(sketch, "E18.bottom", {"start": v(-900, -750) * mm, "end": v(300, -750) * mm});
            skLineSegment(sketch, "E18.top", {"start": v(-900, -1650) * mm, "end": v(300, -1650) * mm});
            skLineSegment(sketch, "E18.left", {"start": v(-900, -750) * mm, "end": v(-900, -1650) * mm});
            skLineSegment(sketch, "E18.right", {"start": v(300, -1200) * mm, "end": v(300, -1650) * mm});
            skLineSegment(sketch, "E19", {"start": v(300, -1200) * mm, "end": v(-900, -1200) * mm, "construction": true});
            skLineSegment(sketch, "E20", {"start": v(300, -750) * mm, "end": v(300, -1650) * mm});
            skLineSegment(sketch, "E21", {"start": v(-300, -1650) * mm, "end": v(-300, -750) * mm, "construction": true});
            skSolve(sketch);
        }
        {
            var Q0;
            {var subQ0=sQuery(id+"F21.wireOp",EDGE,"E18.bottom");Q0=makeQuery(id+"F21.imprint","IMPRINT",FACE,{"disambiguationData":[TD([[makeQuery(id+"F21.imprint","IMPRINT",EDGE,{"derivedFrom":subQ0}),-1.0]])]});}
            extrude(context, id + "F22", {"entities" : qUnion([Q0]), "depth" : 50 * mm, "offsetDistance" : 25 * mm});
        }
        {
            var Q0;
            Q0=makeQuery(id+"F8.opPattern","COPY",BODY,{"derivedFrom":makeQuery(id+"F4.opPattern","COPY",BODY,{"derivedFrom":makeQuery(id+"F3.opPattern","COPY",BODY,{"derivedFrom":makeQuery(id+"F2.opExtrude","SWEPT_BODY",BODY,{"disambiguationData":[OSD([sQuery(id+"F0.wireOp",EDGE,"E0.bottom"),sQuery(id+"F0.wireOp",EDGE,"E0.top"),sQuery(id+"F0.wireOp",EDGE,"E0.left"),sQuery(id+"F0.wireOp",EDGE,"E0.right"),sQuery(id+"F0.wireOp",EDGE,"E1"),sQuery(id+"F0.wireOp",EDGE,"E2"),sQuery(id+"F0.wireOp",EDGE,"E3"),sQuery(id+"F0.wireOp",EDGE,"E4"),sQuery(id+"F1.wireOp",EDGE,"E9.bottom"),sQuery(id+"F1.wireOp",EDGE,"E9.top"),sQuery(id+"F1.wireOp",EDGE,"E9.left"),sQuery(id+"F1.wireOp",EDGE,"E9.right"),sQuery(id+"F1.wireOp",EDGE,"E10"),sQuery(id+"F1.wireOp",EDGE,"E11"),sQuery(id+"F1.wireOp",EDGE,"E14"),sQuery(id+"F1.wireOp",EDGE,"E15")])]}),"instanceName":"1"}),"instanceName":"1"}),"instanceName":"1"});
            transform(context, id + "F23", {"entities" : qUnion([Q0]), "transformType" : TransformType.TRANSLATION_3D, "dx" : -300 * mm, "dy" : 0 * mm, "dz" : 0 * mm, "makeCopy" : false});
        }
        {
            var Q0;
            Q0=makeQuery(id+"F4.opPattern","COPY",BODY,{"derivedFrom":makeQuery(id+"F3.opPattern","COPY",BODY,{"derivedFrom":makeQuery(id+"F2.opExtrude","SWEPT_BODY",BODY,{"disambiguationData":[OSD([sQuery(id+"F0.wireOp",EDGE,"E0.bottom"),sQuery(id+"F0.wireOp",EDGE,"E0.top"),sQuery(id+"F0.wireOp",EDGE,"E0.left"),sQuery(id+"F0.wireOp",EDGE,"E0.right"),sQuery(id+"F0.wireOp",EDGE,"E1"),sQuery(id+"F0.wireOp",EDGE,"E2"),sQuery(id+"F0.wireOp",EDGE,"E3"),sQuery(id+"F0.wireOp",EDGE,"E4"),sQuery(id+"F1.wireOp",EDGE,"E9.bottom"),sQuery(id+"F1.wireOp",EDGE,"E9.top"),sQuery(id+"F1.wireOp",EDGE,"E9.left"),sQuery(id+"F1.wireOp",EDGE,"E9.right"),sQuery(id+"F1.wireOp",EDGE,"E10"),sQuery(id+"F1.wireOp",EDGE,"E11"),sQuery(id+"F1.wireOp",EDGE,"E14"),sQuery(id+"F1.wireOp",EDGE,"E15")])]}),"instanceName":"1"}),"instanceName":"1"});
            transform(context, id + "F24", {"entities" : qUnion([Q0]), "transformType" : TransformType.TRANSLATION_3D, "dx" : -300 * mm, "dy" : 0 * mm, "dz" : 0 * mm, "makeCopy" : false});
        }
        {
            var Q0;
            Q0=makeQuery(id+"F9.opPattern","COPY",BODY,{"derivedFrom":makeQuery(id+"F7.opPattern","COPY",BODY,{"derivedFrom":makeQuery(id+"F3.opPattern","COPY",BODY,{"derivedFrom":makeQuery(id+"F2.opExtrude","SWEPT_BODY",BODY,{"disambiguationData":[OSD([sQuery(id+"F0.wireOp",EDGE,"E0.bottom"),sQuery(id+"F0.wireOp",EDGE,"E0.top"),sQuery(id+"F0.wireOp",EDGE,"E0.left"),sQuery(id+"F0.wireOp",EDGE,"E0.right"),sQuery(id+"F0.wireOp",EDGE,"E1"),sQuery(id+"F0.wireOp",EDGE,"E2"),sQuery(id+"F0.wireOp",EDGE,"E3"),sQuery(id+"F0.wireOp",EDGE,"E4"),sQuery(id+"F1.wireOp",EDGE,"E9.bottom"),sQuery(id+"F1.wireOp",EDGE,"E9.top"),sQuery(id+"F1.wireOp",EDGE,"E9.left"),sQuery(id+"F1.wireOp",EDGE,"E9.right"),sQuery(id+"F1.wireOp",EDGE,"E10"),sQuery(id+"F1.wireOp",EDGE,"E11"),sQuery(id+"F1.wireOp",EDGE,"E14"),sQuery(id+"F1.wireOp",EDGE,"E15")])]}),"instanceName":"1"}),"instanceName":"1"}),"instanceName":"1"});
            transform(context, id + "F25", {"entities" : qUnion([Q0]), "transformType" : TransformType.TRANSLATION_3D, "dx" : 300 * mm, "dy" : 0 * mm, "dz" : 0 * mm, "makeCopy" : false});
        }
        {
            var Q0;
            Q0=makeQuery(id+"F8.opPattern","COPY",BODY,{"derivedFrom":makeQuery(id+"F4.opPattern","COPY",BODY,{"derivedFrom":makeQuery(id+"F3.opPattern","COPY",BODY,{"derivedFrom":makeQuery(id+"F2.opExtrude","SWEPT_BODY",BODY,{"disambiguationData":[OSD([sQuery(id+"F0.wireOp",EDGE,"E0.bottom"),sQuery(id+"F0.wireOp",EDGE,"E0.top"),sQuery(id+"F0.wireOp",EDGE,"E0.left"),sQuery(id+"F0.wireOp",EDGE,"E0.right"),sQuery(id+"F0.wireOp",EDGE,"E1"),sQuery(id+"F0.wireOp",EDGE,"E2"),sQuery(id+"F0.wireOp",EDGE,"E3"),sQuery(id+"F0.wireOp",EDGE,"E4"),sQuery(id+"F1.wireOp",EDGE,"E9.bottom"),sQuery(id+"F1.wireOp",EDGE,"E9.top"),sQuery(id+"F1.wireOp",EDGE,"E9.left"),sQuery(id+"F1.wireOp",EDGE,"E9.right"),sQuery(id+"F1.wireOp",EDGE,"E10"),sQuery(id+"F1.wireOp",EDGE,"E11"),sQuery(id+"F1.wireOp",EDGE,"E14"),sQuery(id+"F1.wireOp",EDGE,"E15")])]}),"instanceName":"1"}),"instanceName":"1"}),"instanceName":"1"});
            transform(context, id + "F26", {"entities" : qUnion([Q0]), "transformType" : TransformType.TRANSLATION_3D, "dx" : 600 * mm, "dy" : 0 * mm, "dz" : 0 * mm, "makeCopy" : true});
        }
        {
            var Q0;
            Q0=makeQuery(id+"F8.opPattern","COPY",BODY,{"derivedFrom":makeQuery(id+"F4.opPattern","COPY",BODY,{"derivedFrom":makeQuery(id+"F3.opPattern","COPY",BODY,{"derivedFrom":makeQuery(id+"F2.opExtrude","SWEPT_BODY",BODY,{"disambiguationData":[OSD([sQuery(id+"F0.wireOp",EDGE,"E0.bottom"),sQuery(id+"F0.wireOp",EDGE,"E0.top"),sQuery(id+"F0.wireOp",EDGE,"E0.left"),sQuery(id+"F0.wireOp",EDGE,"E0.right"),sQuery(id+"F0.wireOp",EDGE,"E1"),sQuery(id+"F0.wireOp",EDGE,"E2"),sQuery(id+"F0.wireOp",EDGE,"E3"),sQuery(id+"F0.wireOp",EDGE,"E4"),sQuery(id+"F1.wireOp",EDGE,"E9.bottom"),sQuery(id+"F1.wireOp",EDGE,"E9.top"),sQuery(id+"F1.wireOp",EDGE,"E9.left"),sQuery(id+"F1.wireOp",EDGE,"E9.right"),sQuery(id+"F1.wireOp",EDGE,"E10"),sQuery(id+"F1.wireOp",EDGE,"E11"),sQuery(id+"F1.wireOp",EDGE,"E14"),sQuery(id+"F1.wireOp",EDGE,"E15")])]}),"instanceName":"1"}),"instanceName":"1"}),"instanceName":"1"});
            transform(context, id + "F27", {"entities" : qUnion([Q0]), "transformType" : TransformType.TRANSLATION_3D, "dx" : 600 * mm, "dy" : -600 * mm, "dz" : 0 * mm, "makeCopy" : true});
        }
        {
            var Q0;
            Q0=makeQuery(id+"F13.opPattern","COPY",BODY,{"derivedFrom":makeQuery(id+"F8.opPattern","COPY",BODY,{"derivedFrom":makeQuery(id+"F4.opPattern","COPY",BODY,{"derivedFrom":makeQuery(id+"F3.opPattern","COPY",BODY,{"derivedFrom":makeQuery(id+"F2.opExtrude","SWEPT_BODY",BODY,{"disambiguationData":[OSD([sQuery(id+"F0.wireOp",EDGE,"E0.bottom"),sQuery(id+"F0.wireOp",EDGE,"E0.top"),sQuery(id+"F0.wireOp",EDGE,"E0.left"),sQuery(id+"F0.wireOp",EDGE,"E0.right"),sQuery(id+"F0.wireOp",EDGE,"E1"),sQuery(id+"F0.wireOp",EDGE,"E2"),sQuery(id+"F0.wireOp",EDGE,"E3"),sQuery(id+"F0.wireOp",EDGE,"E4"),sQuery(id+"F1.wireOp",EDGE,"E9.bottom"),sQuery(id+"F1.wireOp",EDGE,"E9.top"),sQuery(id+"F1.wireOp",EDGE,"E9.left"),sQuery(id+"F1.wireOp",EDGE,"E9.right"),sQuery(id+"F1.wireOp",EDGE,"E10"),sQuery(id+"F1.wireOp",EDGE,"E11"),sQuery(id+"F1.wireOp",EDGE,"E14"),sQuery(id+"F1.wireOp",EDGE,"E15")])]}),"instanceName":"1"}),"instanceName":"1"}),"instanceName":"1"}),"instanceName":"1"});
            transform(context, id + "F28", {"entities" : qUnion([Q0]), "transformType" : TransformType.TRANSLATION_3D, "dx" : 300 * mm, "dy" : 0 * mm, "dz" : 0 * mm, "makeCopy" : false});
        }
        {
            var Q0;
            Q0=makeQuery(id+"F15.opPattern","COPY",BODY,{"derivedFrom":makeQuery(id+"F9.opPattern","COPY",BODY,{"derivedFrom":makeQuery(id+"F7.opPattern","COPY",BODY,{"derivedFrom":makeQuery(id+"F3.opPattern","COPY",BODY,{"derivedFrom":makeQuery(id+"F2.opExtrude","SWEPT_BODY",BODY,{"disambiguationData":[OSD([sQuery(id+"F0.wireOp",EDGE,"E0.bottom"),sQuery(id+"F0.wireOp",EDGE,"E0.top"),sQuery(id+"F0.wireOp",EDGE,"E0.left"),sQuery(id+"F0.wireOp",EDGE,"E0.right"),sQuery(id+"F0.wireOp",EDGE,"E1"),sQuery(id+"F0.wireOp",EDGE,"E2"),sQuery(id+"F0.wireOp",EDGE,"E3"),sQuery(id+"F0.wireOp",EDGE,"E4"),sQuery(id+"F1.wireOp",EDGE,"E9.bottom"),sQuery(id+"F1.wireOp",EDGE,"E9.top"),sQuery(id+"F1.wireOp",EDGE,"E9.left"),sQuery(id+"F1.wireOp",EDGE,"E9.right"),sQuery(id+"F1.wireOp",EDGE,"E10"),sQuery(id+"F1.wireOp",EDGE,"E11"),sQuery(id+"F1.wireOp",EDGE,"E14"),sQuery(id+"F1.wireOp",EDGE,"E15")])]}),"instanceName":"1"}),"instanceName":"1"}),"instanceName":"1"}),"instanceName":"1"});
            transform(context, id + "F29", {"entities" : qUnion([Q0]), "transformType" : TransformType.TRANSLATION_3D, "dx" : -300 * mm, "dy" : 0 * mm, "dz" : 0 * mm, "makeCopy" : false});
        }
        {
            var Q0;
            Q0=makeQuery(id+"F14.opPattern","COPY",BODY,{"derivedFrom":makeQuery(id+"F13.opPattern","COPY",BODY,{"derivedFrom":makeQuery(id+"F8.opPattern","COPY",BODY,{"derivedFrom":makeQuery(id+"F4.opPattern","COPY",BODY,{"derivedFrom":makeQuery(id+"F3.opPattern","COPY",BODY,{"derivedFrom":makeQuery(id+"F2.opExtrude","SWEPT_BODY",BODY,{"disambiguationData":[OSD([sQuery(id+"F0.wireOp",EDGE,"E0.bottom"),sQuery(id+"F0.wireOp",EDGE,"E0.top"),sQuery(id+"F0.wireOp",EDGE,"E0.left"),sQuery(id+"F0.wireOp",EDGE,"E0.right"),sQuery(id+"F0.wireOp",EDGE,"E1"),sQuery(id+"F0.wireOp",EDGE,"E2"),sQuery(id+"F0.wireOp",EDGE,"E3"),sQuery(id+"F0.wireOp",EDGE,"E4"),sQuery(id+"F1.wireOp",EDGE,"E9.bottom"),sQuery(id+"F1.wireOp",EDGE,"E9.top"),sQuery(id+"F1.wireOp",EDGE,"E9.left"),sQuery(id+"F1.wireOp",EDGE,"E9.right"),sQuery(id+"F1.wireOp",EDGE,"E10"),sQuery(id+"F1.wireOp",EDGE,"E11"),sQuery(id+"F1.wireOp",EDGE,"E14"),sQuery(id+"F1.wireOp",EDGE,"E15")])]}),"instanceName":"1"}),"instanceName":"1"}),"instanceName":"1"}),"instanceName":"1"}),"instanceName":"1"});
            transform(context, id + "F30", {"entities" : qUnion([Q0]), "transformType" : TransformType.TRANSLATION_3D, "dx" : 300 * mm, "dy" : 0 * mm, "dz" : 0 * mm, "makeCopy" : false});
        }
        {
            var Q0;
            Q0=makeQuery(id+"F14.opPattern","COPY",BODY,{"derivedFrom":makeQuery(id+"F13.opPattern","COPY",BODY,{"derivedFrom":makeQuery(id+"F8.opPattern","COPY",BODY,{"derivedFrom":makeQuery(id+"F4.opPattern","COPY",BODY,{"derivedFrom":makeQuery(id+"F3.opPattern","COPY",BODY,{"derivedFrom":makeQuery(id+"F2.opExtrude","SWEPT_BODY",BODY,{"disambiguationData":[OSD([sQuery(id+"F0.wireOp",EDGE,"E0.bottom"),sQuery(id+"F0.wireOp",EDGE,"E0.top"),sQuery(id+"F0.wireOp",EDGE,"E0.left"),sQuery(id+"F0.wireOp",EDGE,"E0.right"),sQuery(id+"F0.wireOp",EDGE,"E1"),sQuery(id+"F0.wireOp",EDGE,"E2"),sQuery(id+"F0.wireOp",EDGE,"E3"),sQuery(id+"F0.wireOp",EDGE,"E4"),sQuery(id+"F1.wireOp",EDGE,"E9.bottom"),sQuery(id+"F1.wireOp",EDGE,"E9.top"),sQuery(id+"F1.wireOp",EDGE,"E9.left"),sQuery(id+"F1.wireOp",EDGE,"E9.right"),sQuery(id+"F1.wireOp",EDGE,"E10"),sQuery(id+"F1.wireOp",EDGE,"E11"),sQuery(id+"F1.wireOp",EDGE,"E14"),sQuery(id+"F1.wireOp",EDGE,"E15")])]}),"instanceName":"1"}),"instanceName":"1"}),"instanceName":"1"}),"instanceName":"1"}),"instanceName":"1"});
            transform(context, id + "F31", {"entities" : qUnion([Q0]), "transformType" : TransformType.TRANSLATION_3D, "dx" : -600 * mm, "dy" : 0 * mm, "dz" : 0 * mm, "makeCopy" : true});
        }
        {
            var Q0;
            Q0=makeQuery(id+"F14.opPattern","COPY",BODY,{"derivedFrom":makeQuery(id+"F13.opPattern","COPY",BODY,{"derivedFrom":makeQuery(id+"F8.opPattern","COPY",BODY,{"derivedFrom":makeQuery(id+"F4.opPattern","COPY",BODY,{"derivedFrom":makeQuery(id+"F3.opPattern","COPY",BODY,{"derivedFrom":makeQuery(id+"F2.opExtrude","SWEPT_BODY",BODY,{"disambiguationData":[OSD([sQuery(id+"F0.wireOp",EDGE,"E0.bottom"),sQuery(id+"F0.wireOp",EDGE,"E0.top"),sQuery(id+"F0.wireOp",EDGE,"E0.left"),sQuery(id+"F0.wireOp",EDGE,"E0.right"),sQuery(id+"F0.wireOp",EDGE,"E1"),sQuery(id+"F0.wireOp",EDGE,"E2"),sQuery(id+"F0.wireOp",EDGE,"E3"),sQuery(id+"F0.wireOp",EDGE,"E4"),sQuery(id+"F1.wireOp",EDGE,"E9.bottom"),sQuery(id+"F1.wireOp",EDGE,"E9.top"),sQuery(id+"F1.wireOp",EDGE,"E9.left"),sQuery(id+"F1.wireOp",EDGE,"E9.right"),sQuery(id+"F1.wireOp",EDGE,"E10"),sQuery(id+"F1.wireOp",EDGE,"E11"),sQuery(id+"F1.wireOp",EDGE,"E14"),sQuery(id+"F1.wireOp",EDGE,"E15")])]}),"instanceName":"1"}),"instanceName":"1"}),"instanceName":"1"}),"instanceName":"1"}),"instanceName":"1"});
            transform(context, id + "F32", {"entities" : qUnion([Q0]), "transformType" : TransformType.TRANSLATION_3D, "dx" : -600 * mm, "dy" : -600 * mm, "dz" : 0 * mm, "makeCopy" : true});
        }
    });
